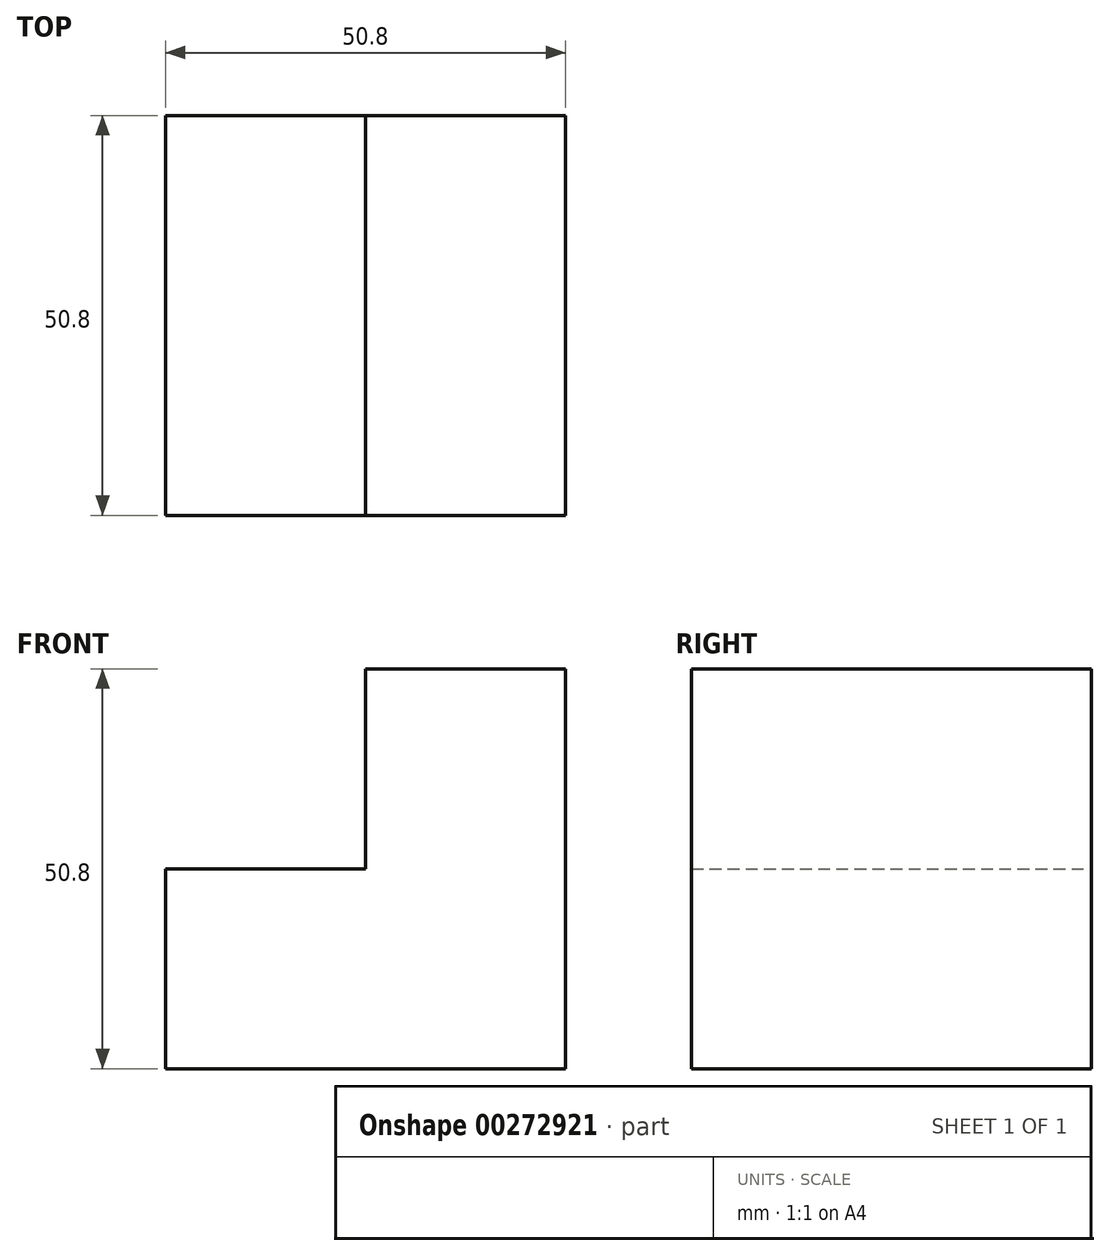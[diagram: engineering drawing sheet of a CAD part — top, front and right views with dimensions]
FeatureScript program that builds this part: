
annotation { "Feature Type Name" : "Feature", "Feature Type Description" : "" }
export const myFeature = defineFeature(function(context is Context, id is Id, definition is map)
    precondition{}
    {
        {
            var Q0;
            Q0=qCreatedBy(makeId("Front.planeOp"),FACE);
            var sketch = newSketch(context, id + "F0", { "sketchPlane" : qUnion([Q0])});
            skLineSegment(sketch, "E0", {"start": v(0, 0) * mm, "end": v(-50.8, 0) * mm});
            skLineSegment(sketch, "E1", {"start": v(0, 0) * mm, "end": v(0, 50.8) * mm});
            skLineSegment(sketch, "E2", {"start": v(0, 50.8) * mm, "end": v(-25.4, 50.8) * mm});
            skLineSegment(sketch, "E3", {"start": v(-25.4, 50.8) * mm, "end": v(-25.4, 25.4) * mm});
            skLineSegment(sketch, "E4", {"start": v(-25.4, 25.4) * mm, "end": v(-50.8, 25.4) * mm});
            skLineSegment(sketch, "E5", {"start": v(-50.8, 25.4) * mm, "end": v(-50.8, 0) * mm});
            skSolve(sketch);
        }
        {
            var Q0;
            Q0=makeQuery(id+"F0.imprint","IMPRINT",FACE,{"disambiguationData":[TD([[makeQuery(id+"F0.imprint","IMPRINT",EDGE,{"derivedFrom":sQuery(id+"F0.wireOp",EDGE,"E0")}),-1.0]])]});
            extrude(context, id + "F1", {"entities" : qUnion([Q0]), "depth" : 50.8 * mm});
        }
    });
